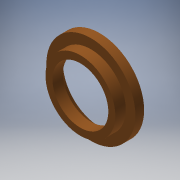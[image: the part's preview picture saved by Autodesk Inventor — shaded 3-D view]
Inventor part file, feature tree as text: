
AUTODESK INVENTOR PART (.ipt)
format: ipt  version: 2018 (Build 220112000, 112)  size: 144,896 bytes
history: native  units: mm (DEFAULTED — no unit token found)
features: revolve x1, chamfer x1, sketch x1
ambient origin geometry x8: Origin, YZ Plane, XZ Plane, XY Plane, X Axis, Y Axis, Z Axis, Center Point
bodies: Solid1 (feature_tree)
feature tree (3):
  revolve  "Revolution1"  [1 undecoded]
  chamfer  "Chamfer1"  Distance=40.0mm
  sketch  "Sketch1"  dims[d0=32.0mm d1=51.0mm d2=40.0mm d3=5.0mm d4=11.0mm d5=90.0deg d6=5.0mm d7=2.0mm d8=45.0deg]
note: 1 required parameter value undecoded (feature->parameter linkage not recoverable at this tier; creation-order binding heuristic only, values carry confidence <= 0.55)
